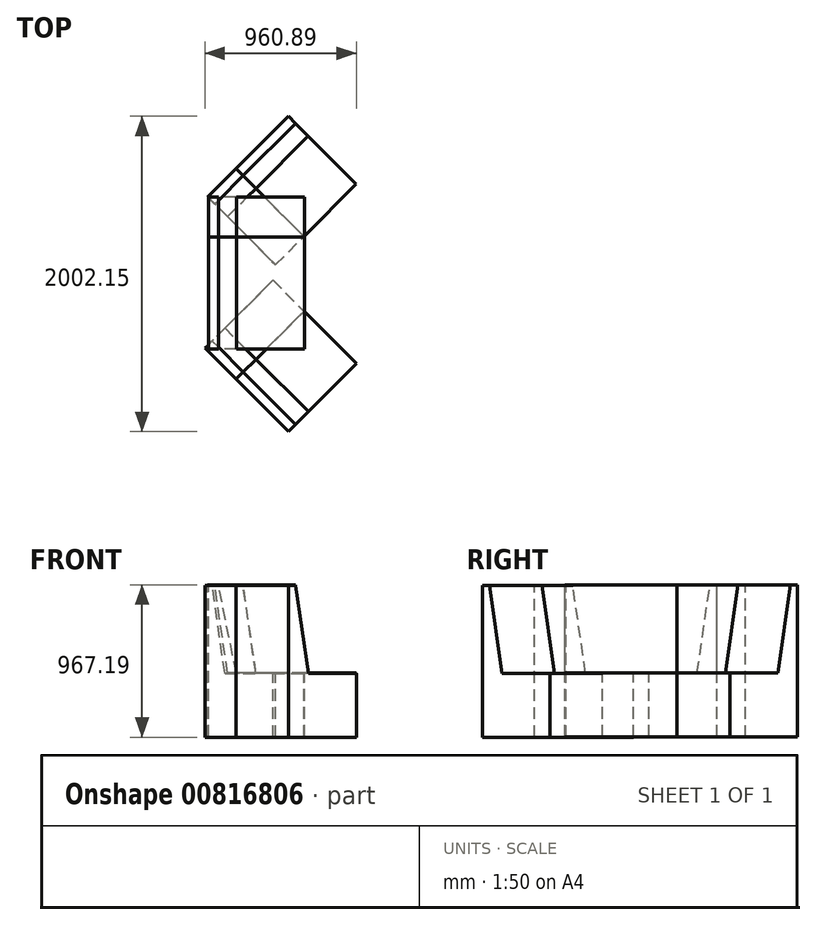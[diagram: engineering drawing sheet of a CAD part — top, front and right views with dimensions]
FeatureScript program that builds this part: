
annotation { "Feature Type Name" : "Feature", "Feature Type Description" : "" }
export const myFeature = defineFeature(function(context is Context, id is Id, definition is map)
    precondition{}
    {
        {
            var Q0;
            Q0=qCreatedBy(makeId("Front.planeOp"),FACE);
            var sketch = newSketch(context, id + "F0", { "sketchPlane" : qUnion([Q0])});
            skLineSegment(sketch, "E0", {"start": v(0, 0) * mm, "end": v(0, 965.2) * mm});
            skLineSegment(sketch, "E1", {"start": v(0, 965.2) * mm, "end": v(63.5, 965.2) * mm});
            skLineSegment(sketch, "E2", {"start": v(0, 0) * mm, "end": v(609.6, 0) * mm});
            skLineSegment(sketch, "E3", {"start": v(609.6, 0) * mm, "end": v(609.6, 406.4) * mm});
            skLineSegment(sketch, "E4", {"start": v(609.6, 406.4) * mm, "end": v(177.8, 406.4) * mm});
            skLineSegment(sketch, "E5", {"start": v(177.8, 406.4) * mm, "end": v(63.5, 965.2) * mm});
            skSolve(sketch);
        }
        {
            var Q0;
            Q0=makeQuery(id+"F0.imprint","IMPRINT",FACE,{"disambiguationData":[TD([[makeQuery(id+"F0.imprint","IMPRINT",EDGE,{"derivedFrom":sQuery(id+"F0.wireOp",EDGE,"E0")}),-1.0]])]});
            extrude(context, id + "F1", {"entities" : qUnion([Q0]), "depth" : 711.2 * mm, "offsetDistance" : 25.4 * mm});
        }
        {
            var Q0;
            Q0=qCreatedBy(makeId("Top.planeOp"),FACE);
            var sketch = newSketch(context, id + "F2", { "sketchPlane" : qUnion([Q0])});
            skLineSegment(sketch, "E6", {"start": v(610.09, 0) * mm, "end": v(287.7, 322.38) * mm});
            skSolve(sketch);
        }
        {
            var Q0;
            Q0=sQuery(id+"F2.wireOp",EDGE,"E6");
            cPlane(context, id + "F3", {"entities" : qUnion([Q0]), "cplaneType" : CPlaneType.LINE_ANGLE, "offset" : 25.4 * mm, "angle" : 270 * degree, "width" : 152.4 * mm, "height" : 152.4 * mm});
        }
        {
            var Q0;
            Q0=qCreatedBy(id+"F3.planeOp",FACE);
            var sketch = newSketch(context, id + "F4", { "sketchPlane" : qUnion([Q0])});
            skLineSegment(sketch, "E7", {"start": v(-182.83, -0.83) * mm, "end": v(-182.83, 964.37) * mm});
            skLineSegment(sketch, "E8", {"start": v(-182.83, 964.37) * mm, "end": v(-119.33, 964.37) * mm});
            skLineSegment(sketch, "E9", {"start": v(-182.83, -0.83) * mm, "end": v(426.77, -0.83) * mm});
            skLineSegment(sketch, "E10", {"start": v(426.77, -0.83) * mm, "end": v(426.77, 405.57) * mm});
            skLineSegment(sketch, "E11", {"start": v(426.77, 405.57) * mm, "end": v(-5.03, 405.57) * mm});
            skLineSegment(sketch, "E12", {"start": v(-5.03, 405.57) * mm, "end": v(-119.33, 964.37) * mm});
            skSolve(sketch);
        }
        {
            var Q0;
            Q0 = qSketchRegion(id + "F4", true);
            extrude(context, id + "F5", {"entities" : qUnion([Q0]), "oppositeDirection" : true, "depth" : 469.9 * mm, "offsetDistance" : 25.4 * mm});
        }
        {
            var Q0;
            Q0=qCreatedBy(makeId("Top.planeOp"),FACE);
            var sketch = newSketch(context, id + "F6", { "sketchPlane" : qUnion([Q0])});
            skLineSegment(sketch, "E13", {"start": v(609.85, -470.45) * mm, "end": v(441.53, -638.78) * mm});
            skSolve(sketch);
        }
        {
            var Q0;
            Q0 = qBodyType(qCreatedBy(id + "F6" ,EDGE), BodyType.WIRE);
            cPlane(context, id + "F7", {"entities" : qUnion([Q0]), "cplaneType" : CPlaneType.LINE_ANGLE, "offset" : 25.4 * mm, "angle" : 90 * degree, "width" : 152.4 * mm, "height" : 152.4 * mm});
        }
        {
            var Q0;
            Q0=qCreatedBy(id+"F7.planeOp",FACE);
            var sketch = newSketch(context, id + "F8", { "sketchPlane" : qUnion([Q0])});
            skLineSegment(sketch, "E14", {"start": v(-513.55, -1.99) * mm, "end": v(-513.55, 963.21) * mm});
            skLineSegment(sketch, "E15", {"start": v(-513.55, 963.21) * mm, "end": v(-450.05, 963.21) * mm});
            skLineSegment(sketch, "E16", {"start": v(-513.55, -1.99) * mm, "end": v(96.05, -1.99) * mm});
            skLineSegment(sketch, "E17", {"start": v(96.05, -1.99) * mm, "end": v(96.05, 404.41) * mm});
            skLineSegment(sketch, "E18", {"start": v(96.05, 404.41) * mm, "end": v(-335.75, 404.41) * mm});
            skLineSegment(sketch, "E19", {"start": v(-335.75, 404.41) * mm, "end": v(-450.05, 963.21) * mm});
            skSolve(sketch);
        }
        {
            var Q0;
            Q0 = qSketchRegion(id + "F8", true);
            extrude(context, id + "F9", {"entities" : qUnion([Q0]), "depth" : 469.9 * mm, "offsetDistance" : 25.4 * mm});
        }
        {
            var Q0;
            Q0=makeQuery(id+"F9.opExtrude","CAP_FACE",FACE,{"disambiguationData":[OSD([sQuery(id+"F8.wireOp",EDGE,"E14"),sQuery(id+"F8.wireOp",EDGE,"E15"),sQuery(id+"F8.wireOp",EDGE,"E16"),sQuery(id+"F8.wireOp",EDGE,"E17"),sQuery(id+"F8.wireOp",EDGE,"E18"),sQuery(id+"F8.wireOp",EDGE,"E19")])],"isStart":true});
            extrude(context, id + "F10", {"entities" : qUnion([Q0]), "depth" : 279.4 * mm, "offsetDistance" : 25.4 * mm});
        }
        {
            var Q0;
            Q0=makeQuery(id+"F5.opExtrude","CAP_FACE",FACE,{"disambiguationData":[OSD([sQuery(id+"F4.wireOp",EDGE,"E7"),sQuery(id+"F4.wireOp",EDGE,"E8"),sQuery(id+"F4.wireOp",EDGE,"E9"),sQuery(id+"F4.wireOp",EDGE,"E10"),sQuery(id+"F4.wireOp",EDGE,"E11"),sQuery(id+"F4.wireOp",EDGE,"E12")])],"isStart":true});
            extrude(context, id + "F11", {"entities" : qUnion([Q0]), "depth" : 254 * mm, "offsetDistance" : 25.4 * mm});
        }
        {
            var Q0;
            Q0=makeQuery(id+"F1.opExtrude","CAP_FACE",FACE,{"disambiguationData":[OSD([sQuery(id+"F0.wireOp",EDGE,"E0"),sQuery(id+"F0.wireOp",EDGE,"E1"),sQuery(id+"F0.wireOp",EDGE,"E2"),sQuery(id+"F0.wireOp",EDGE,"E3"),sQuery(id+"F0.wireOp",EDGE,"E4"),sQuery(id+"F0.wireOp",EDGE,"E5")])],"isStart":true});
            extrude(context, id + "F12", {"entities" : qUnion([Q0]), "depth" : 254 * mm, "offsetDistance" : 25.4 * mm});
        }
    });
